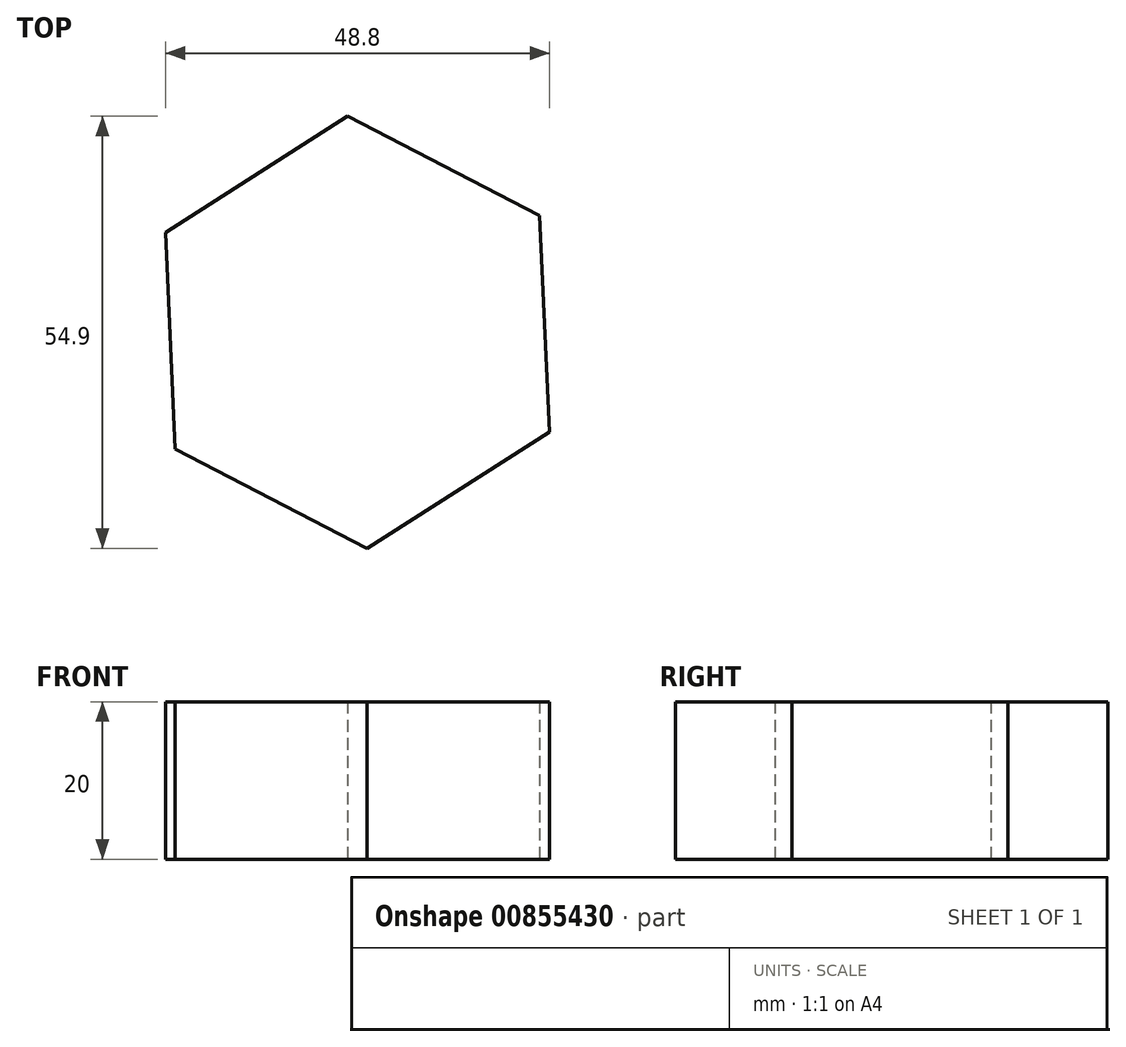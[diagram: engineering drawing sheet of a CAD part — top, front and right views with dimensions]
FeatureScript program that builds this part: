
annotation { "Feature Type Name" : "Feature", "Feature Type Description" : "" }
export const myFeature = defineFeature(function(context is Context, id is Id, definition is map)
    precondition{}
    {
        {
            var Q0;
            Q0=qCreatedBy(makeId("Top.planeOp"),FACE);
            var sketch = newSketch(context, id + "F0", { "sketchPlane" : qUnion([Q0])});
            skCircle(sketch, "E0.cCircle", {"center": v(0, 0) * mm, "radius": 23.8 * mm, "construction": true});
            skLineSegment(sketch, "E0.0", {"start": v(-1.24, 27.45) * mm, "end": v(23.15, 14.8) * mm});
            skLineSegment(sketch, "E0.1", {"start": v(23.15, 14.8) * mm, "end": v(24.4, -12.65) * mm});
            skLineSegment(sketch, "E0.2", {"start": v(24.4, -12.65) * mm, "end": v(1.24, -27.45) * mm});
            skLineSegment(sketch, "E0.3", {"start": v(1.24, -27.45) * mm, "end": v(-23.15, -14.8) * mm});
            skLineSegment(sketch, "E0.4", {"start": v(-23.15, -14.8) * mm, "end": v(-24.4, 12.65) * mm});
            skLineSegment(sketch, "E0.5", {"start": v(-24.4, 12.65) * mm, "end": v(-1.24, 27.45) * mm});
            skPoint(sketch, "E0.0.midPoint", {"position": v(10.96, 21.13) * mm});
            skSolve(sketch);
        }
        {
            var Q0;
            Q0=makeQuery(id+"F0.imprint","IMPRINT",FACE,{"disambiguationData":[TD([[makeQuery(id+"F0.imprint","IMPRINT",EDGE,{"derivedFrom":sQuery(id+"F0.wireOp",EDGE,"E0.0")}),-1.0]])]});
            extrude(context, id + "F1", {"entities" : qUnion([Q0]), "depth" : 20 * mm, "offsetDistance" : 25.4 * mm});
        }
    });
